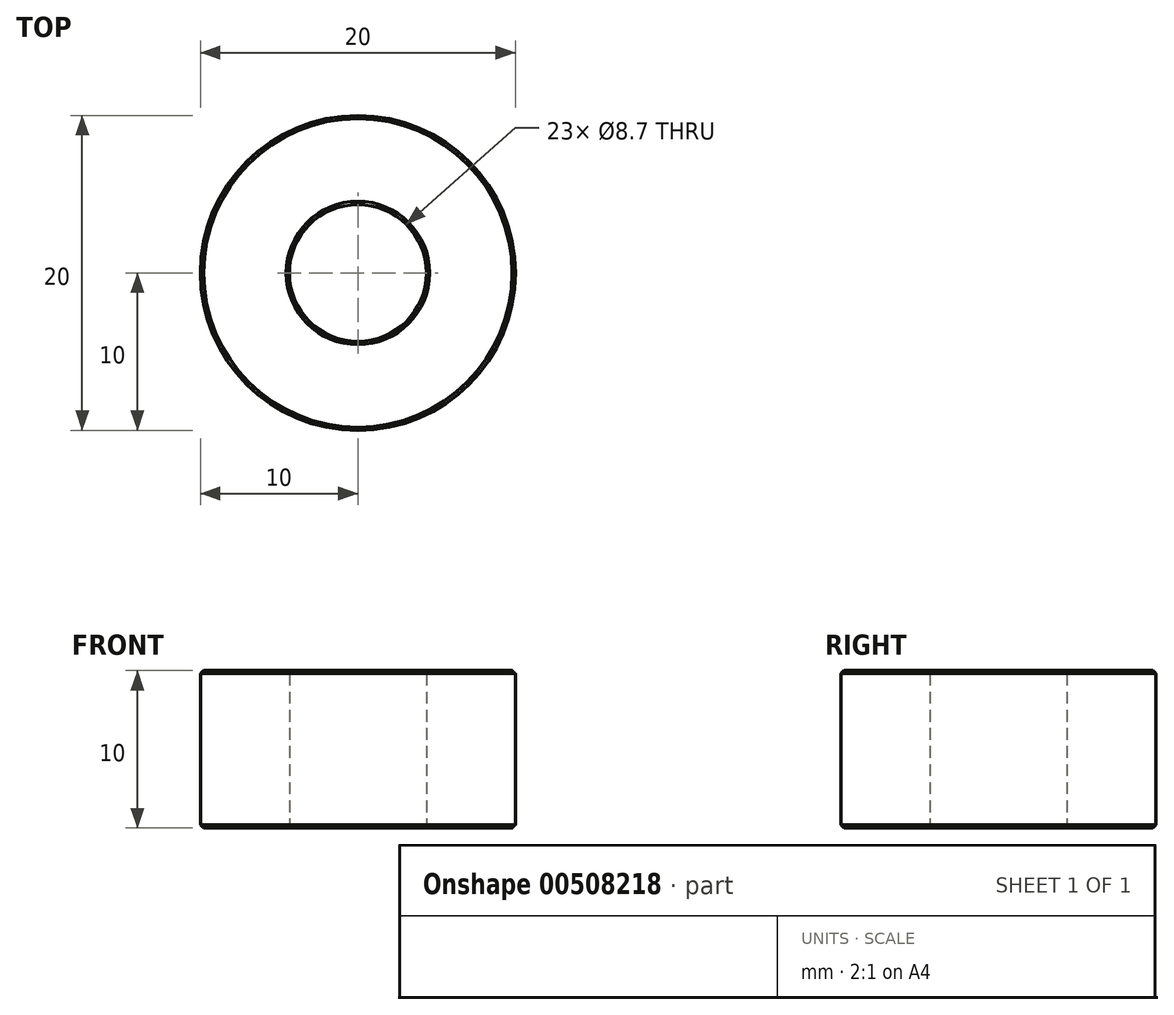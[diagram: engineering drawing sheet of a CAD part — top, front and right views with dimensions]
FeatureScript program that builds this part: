
annotation { "Feature Type Name" : "Feature", "Feature Type Description" : "" }
export const myFeature = defineFeature(function(context is Context, id is Id, definition is map)
    precondition{}
    {
        {
            var Q0;
            Q0=qCreatedBy(makeId("Top.planeOp"),FACE);
            var sketch = newSketch(context, id + "F0", { "sketchPlane" : qUnion([Q0])});
            skCircle(sketch, "E0", {"center": v(0, 0) * mm, "radius": 10 * mm});
            skCircle(sketch, "E1", {"center": v(0, 0) * mm, "radius": 4.35 * mm});
            skSolve(sketch);
        }
        {
            var Q0;
            Q0=makeQuery(id+"F0.imprint","IMPRINT",FACE,{"disambiguationData":[TD([[makeQuery(id+"F0.imprint","IMPRINT",EDGE,{"derivedFrom":sQuery(id+"F0.wireOp",EDGE,"E0")}),1.0]])]});
            extrude(context, id + "F1", {"entities" : qUnion([Q0]), "depth" : 10 * mm, "offsetDistance" : 25 * mm});
        }
        {
            var Q0;
            Q0=makeQuery(id+"F1.opExtrude","CAP_FACE",FACE,{"disambiguationData":[OSD([sQuery(id+"F0.wireOp",EDGE,"E0"),sQuery(id+"F0.wireOp",EDGE,"E1")])],"isStart":false});
            var Q1;
            Q1=makeQuery(id+"F1.opExtrude","CAP_FACE",FACE,{"disambiguationData":[OSD([sQuery(id+"F0.wireOp",EDGE,"E0"),sQuery(id+"F0.wireOp",EDGE,"E1")])],"isStart":true});
            chamfer(context, id + "F2", {"entities" : qUnion([Q0, Q1]), "width" : 0.2 * mm, "tangentPropagation" : true});
        }
    });
